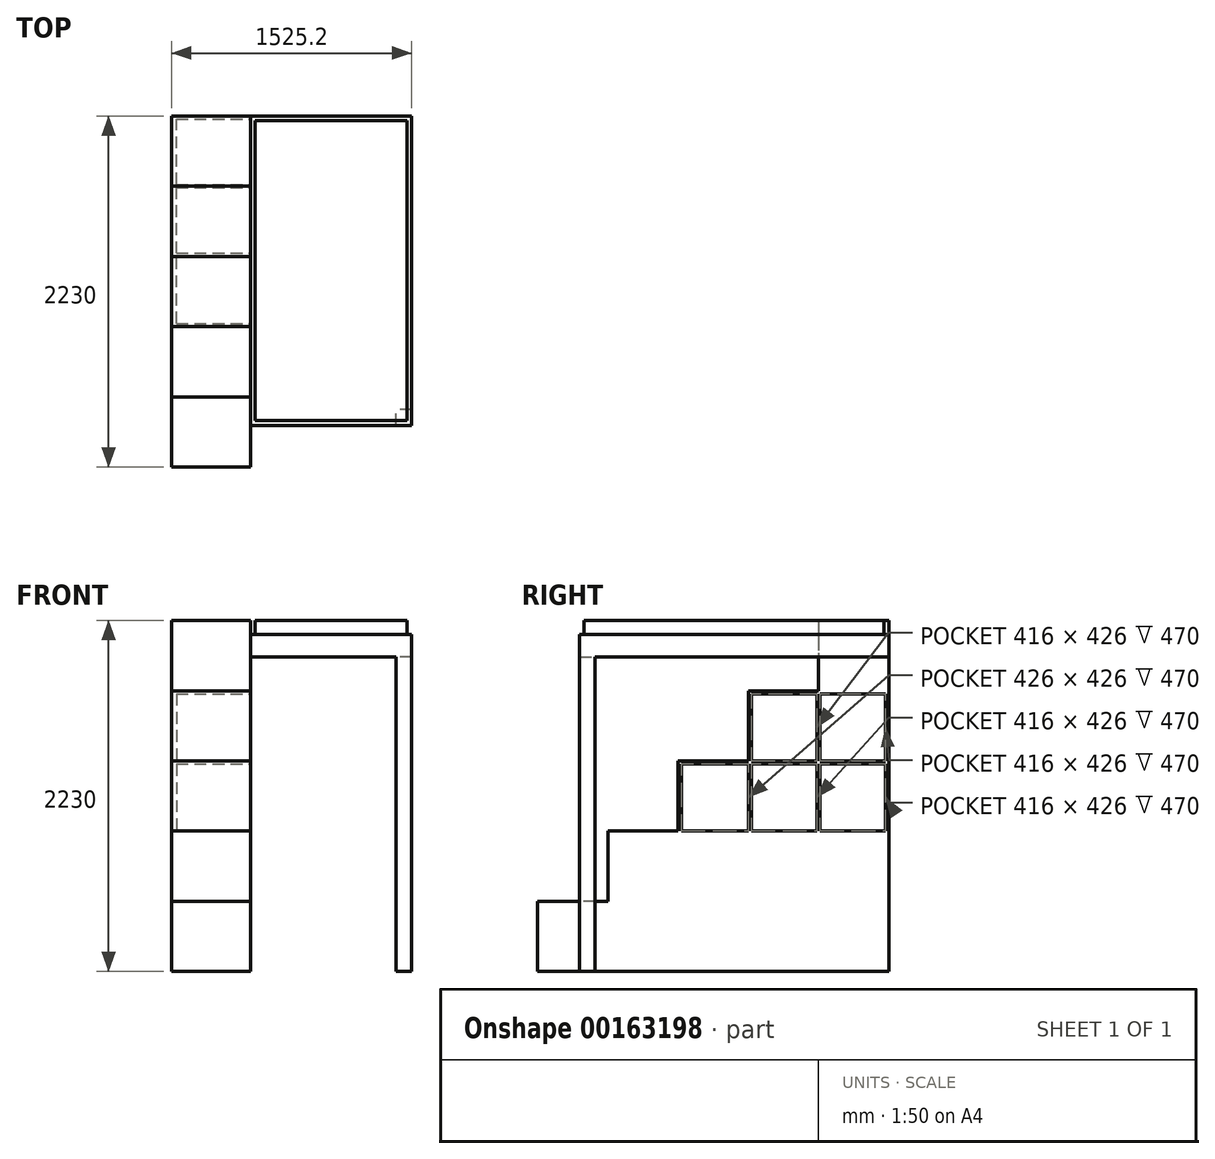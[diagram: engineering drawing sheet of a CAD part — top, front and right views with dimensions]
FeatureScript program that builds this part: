
annotation { "Feature Type Name" : "Feature", "Feature Type Description" : "" }
export const myFeature = defineFeature(function(context is Context, id is Id, definition is map)
    precondition{}
    {
        {
            var Q0;
            Q0=qCreatedBy(makeId("Top.planeOp"),FACE);
            var sketch = newSketch(context, id + "F0", { "sketchPlane" : qUnion([Q0])});
            skLineSegment(sketch, "E0.bottom", {"start": v(-482.6, 952.5) * mm, "end": v(482.6, 952.5) * mm});
            skLineSegment(sketch, "E0.top", {"start": v(-482.6, -952.5) * mm, "end": v(482.6, -952.5) * mm});
            skLineSegment(sketch, "E0.left", {"start": v(-482.6, 952.5) * mm, "end": v(-482.6, -952.5) * mm});
            skLineSegment(sketch, "E0.right", {"start": v(482.6, 952.5) * mm, "end": v(482.6, -952.5) * mm});
            skPoint(sketch, "E0.middle", {"position": v(0, 0) * mm});
            skSolve(sketch);
        }
        {
            var Q0;
            Q0 = qSketchRegion(id + "F0", true);
            extrude(context, id + "F1", {"entities" : qUnion([Q0]), "endBound" : BoundingType.SYMMETRIC, "depth" : 200 * mm});
        }
        {
            var Q0;
            Q0=makeQuery(id+"F1.opExtrude","CAP_FACE",FACE,{"disambiguationData":[OSD([sQuery(id+"F0.wireOp",EDGE,"E0.bottom"),sQuery(id+"F0.wireOp",EDGE,"E0.top"),sQuery(id+"F0.wireOp",EDGE,"E0.left"),sQuery(id+"F0.wireOp",EDGE,"E0.right")])],"isStart":true});
            var sketch = newSketch(context, id + "F2", { "sketchPlane" : qUnion([Q0])});
            skLineSegment(sketch, "E1.0.0", {"start": v(-482.6, -952.5) * mm, "end": v(482.6, -952.5) * mm});
            skLineSegment(sketch, "E1.0.1", {"start": v(482.6, -952.5) * mm, "end": v(482.6, 952.5) * mm});
            skLineSegment(sketch, "E1.0.2", {"start": v(482.6, 952.5) * mm, "end": v(-482.6, 952.5) * mm});
            skLineSegment(sketch, "E1.0.3", {"start": v(-482.6, 952.5) * mm, "end": v(-482.6, -952.5) * mm});
            skLineSegment(sketch, "E2.0", {"start": v(-512.6, -982.5) * mm, "end": v(512.6, -982.5) * mm});
            skLineSegment(sketch, "E2.1", {"start": v(-512.6, 982.5) * mm, "end": v(-512.6, -982.5) * mm});
            skLineSegment(sketch, "E2.2", {"start": v(512.6, 982.5) * mm, "end": v(-512.6, 982.5) * mm});
            skLineSegment(sketch, "E2.3", {"start": v(512.6, -982.5) * mm, "end": v(512.6, 982.5) * mm});
            skSolve(sketch);
        }
        {
            var Q0;
            Q0 = qSketchRegion(id + "F2", true);
            extrude(context, id + "F3", {"entities" : qUnion([Q0]), "oppositeDirection" : true, "depth" : 110 * mm});
        }
        {
            var Q0;
            Q0=makeQuery(id+"F3.opExtrude","CAP_FACE",FACE,{"disambiguationData":[OSD([sQuery(id+"F2.wireOp",EDGE,"E1.0.0"),sQuery(id+"F2.wireOp",EDGE,"E1.0.1"),sQuery(id+"F2.wireOp",EDGE,"E1.0.2"),sQuery(id+"F2.wireOp",EDGE,"E1.0.3"),sQuery(id+"F2.wireOp",EDGE,"E2.0"),sQuery(id+"F2.wireOp",EDGE,"E2.1"),sQuery(id+"F2.wireOp",EDGE,"E2.2"),sQuery(id+"F2.wireOp",EDGE,"E2.3")])],"isStart":true});
            var sketch = newSketch(context, id + "F4", { "sketchPlane" : qUnion([Q0])});
            skLineSegment(sketch, "E3.0", {"start": v(-512.6, 982.5) * mm, "end": v(-512.6, -982.5) * mm});
            skLineSegment(sketch, "E4.0", {"start": v(512.6, 982.5) * mm, "end": v(-512.6, 982.5) * mm});
            skLineSegment(sketch, "E5.0", {"start": v(512.6, -982.5) * mm, "end": v(512.6, 982.5) * mm});
            skLineSegment(sketch, "E6.0", {"start": v(-512.6, -982.5) * mm, "end": v(512.6, -982.5) * mm});
            skSolve(sketch);
        }
        {
            var Q0;
            Q0 = qSketchRegion(id + "F4", true);
            extrude(context, id + "F5", {"entities" : qUnion([Q0]), "operationType" : NewBodyOperationType.ADD, "depth" : 30 * mm});
        }
        {
            var Q0;
            Q0=makeQuery(id+"F5.boolean.opBoolean","MERGE",FACE,{"derivedFrom":[makeQuery(id+"F3.opExtrude","SWEPT_FACE",FACE,{"disambiguationData":[OSD([sQuery(id+"F2.wireOp",EDGE,"E2.1")])]}),makeQuery(id+"F5.opExtrude","SWEPT_FACE",FACE,{"disambiguationData":[OSD([sQuery(id+"F4.wireOp",EDGE,"E3.0")])]})]});
            var sketch = newSketch(context, id + "F6", { "sketchPlane" : qUnion([Q0])});
            skLineSegment(sketch, "E7", {"start": v(-982.5, 100) * mm, "end": v(-982.5, -2130) * mm});
            skLineSegment(sketch, "E8", {"start": v(-982.5, 100) * mm, "end": v(-536.5, 100) * mm});
            skLineSegment(sketch, "E9", {"start": v(-536.5, 100) * mm, "end": v(-536.5, -346) * mm});
            skLineSegment(sketch, "E10", {"start": v(-536.5, -346) * mm, "end": v(-90.5, -346) * mm});
            skLineSegment(sketch, "E11", {"start": v(-90.5, -346) * mm, "end": v(-90.5, -792) * mm});
            skLineSegment(sketch, "E12", {"start": v(-90.5, -792) * mm, "end": v(355.5, -792) * mm});
            skLineSegment(sketch, "E13", {"start": v(355.5, -792) * mm, "end": v(355.5, -1238) * mm});
            skLineSegment(sketch, "E14", {"start": v(355.5, -1238) * mm, "end": v(801.5, -1238) * mm});
            skLineSegment(sketch, "E15", {"start": v(801.5, -1238) * mm, "end": v(801.5, -1684) * mm});
            skLineSegment(sketch, "E16", {"start": v(801.5, -1684) * mm, "end": v(1247.5, -1684) * mm});
            skLineSegment(sketch, "E17", {"start": v(1247.5, -1684) * mm, "end": v(1247.5, -2130) * mm});
            skLineSegment(sketch, "E18", {"start": v(-982.5, -2130) * mm, "end": v(1247.5, -2130) * mm});
            skSolve(sketch);
        }
        {
            var Q0;
            Q0 = qSketchRegion(id + "F6", true);
            extrude(context, id + "F7", {"entities" : qUnion([Q0]), "operationType" : NewBodyOperationType.ADD, "depth" : 500 * mm});
        }
        {
            var Q0;
            Q0=makeQuery(id+"F5.opExtrude","CAP_FACE",FACE,{"disambiguationData":[OSD([sQuery(id+"F4.wireOp",EDGE,"E3.0"),sQuery(id+"F4.wireOp",EDGE,"E4.0"),sQuery(id+"F4.wireOp",EDGE,"E5.0"),sQuery(id+"F4.wireOp",EDGE,"E6.0")])],"isStart":false});
            var sketch = newSketch(context, id + "F8", { "sketchPlane" : qUnion([Q0])});
            skLineSegment(sketch, "E19.bottom", {"start": v(512.6, 982.5) * mm, "end": v(412.6, 982.5) * mm});
            skLineSegment(sketch, "E19.top", {"start": v(512.6, 882.5) * mm, "end": v(412.6, 882.5) * mm});
            skLineSegment(sketch, "E19.left", {"start": v(512.6, 982.5) * mm, "end": v(512.6, 882.5) * mm});
            skLineSegment(sketch, "E19.right", {"start": v(412.6, 982.5) * mm, "end": v(412.6, 882.5) * mm});
            skSolve(sketch);
        }
        {
            var Q0;
            Q0 = qSketchRegion(id + "F8", true);
            var Q1;
            Q1=makeQuery(id+"F7.opExtrude","SWEPT_FACE",FACE,{"disambiguationData":[OSD([sQuery(id+"F6.wireOp",EDGE,"E18")])]});
            extrude(context, id + "F9", {"entities" : qUnion([Q0]), "operationType" : NewBodyOperationType.ADD, "endBound" : BoundingType.UP_TO_SURFACE, "endBoundEntityFace" : qUnion([Q1]), "depth" : 25 * mm});
        }
        {
            var Q0;
            {var subQ0=sQuery(id+"F6.wireOp",EDGE,"E12");var subQ1=sQuery(id+"F6.wireOp",EDGE,"E11");var subQ2=sQuery(id+"F6.wireOp",EDGE,"E10");var subQ4=sQuery(id+"F6.wireOp",EDGE,"E7");var subQ6=sQuery(id+"F6.wireOp",EDGE,"E9");var subQ7=sQuery(id+"F6.wireOp",EDGE,"E16");var subQ8=sQuery(id+"F6.wireOp",EDGE,"E13");var subQ9=sQuery(id+"F6.wireOp",EDGE,"E14");var subQ10=sQuery(id+"F6.wireOp",EDGE,"E15");var subQ11=sQuery(id+"F6.wireOp",EDGE,"E17");var subQ12=sQuery(id+"F6.wireOp",EDGE,"E18");Q0=makeQuery(id+"F7.boolean.opBoolean","SPLIT",FACE,{"disambiguationData":[TD([makeQuery(id+"F7.opExtrude","SWEPT_FACE",FACE,{"disambiguationData":[OSD([subQ2])]})])],"derivedFrom":makeQuery(id+"F7.opExtrude","CAP_FACE",FACE,{"disambiguationData":[OSD([subQ4,sQuery(id+"F6.wireOp",EDGE,"E8"),subQ6,subQ2,subQ1,subQ0,subQ8,subQ9,subQ10,subQ7,subQ11,subQ12])],"isStart":true})});}
            var sketch = newSketch(context, id + "F10", { "sketchPlane" : qUnion([Q0])});
            skLineSegment(sketch, "E20.bottom", {"start": v(110.5, -366) * mm, "end": v(526.5, -366) * mm});
            skLineSegment(sketch, "E20.top", {"start": v(110.5, -792) * mm, "end": v(526.5, -792) * mm});
            skLineSegment(sketch, "E20.left", {"start": v(110.5, -366) * mm, "end": v(110.5, -792) * mm});
            skLineSegment(sketch, "E20.right", {"start": v(526.5, -366) * mm, "end": v(526.5, -792) * mm});
            skLineSegment(sketch, "E21.bottom", {"start": v(-335.5, -812) * mm, "end": v(90.5, -812) * mm});
            skLineSegment(sketch, "E21.top", {"start": v(-335.5, -1238) * mm, "end": v(90.5, -1238) * mm});
            skLineSegment(sketch, "E21.left", {"start": v(-335.5, -812) * mm, "end": v(-335.5, -1238) * mm});
            skLineSegment(sketch, "E21.right", {"start": v(90.5, -812) * mm, "end": v(90.5, -1238) * mm});
            skLineSegment(sketch, "E22.bottom", {"start": v(110.5, -812) * mm, "end": v(526.5, -812) * mm});
            skLineSegment(sketch, "E22.top", {"start": v(110.5, -1238) * mm, "end": v(526.5, -1238) * mm});
            skLineSegment(sketch, "E22.left", {"start": v(110.5, -812) * mm, "end": v(110.5, -1238) * mm});
            skLineSegment(sketch, "E22.right", {"start": v(526.5, -812) * mm, "end": v(526.5, -1238) * mm});
            skLineSegment(sketch, "E23.bottom", {"start": v(90.5, -792) * mm, "end": v(110.5, -792) * mm, "construction": true});
            skLineSegment(sketch, "E23.top", {"start": v(90.5, -812) * mm, "end": v(110.5, -812) * mm, "construction": true});
            skLineSegment(sketch, "E23.left", {"start": v(90.5, -792) * mm, "end": v(90.5, -812) * mm, "construction": true});
            skLineSegment(sketch, "E23.right", {"start": v(110.5, -792) * mm, "end": v(110.5, -812) * mm, "construction": true});
            skLineSegment(sketch, "E24.bottom", {"start": v(-335.5, -812) * mm, "end": v(-355.5, -812) * mm, "construction": true});
            skLineSegment(sketch, "E24.top", {"start": v(-335.5, -792) * mm, "end": v(-355.5, -792) * mm, "construction": true});
            skLineSegment(sketch, "E24.left", {"start": v(-335.5, -812) * mm, "end": v(-335.5, -792) * mm, "construction": true});
            skLineSegment(sketch, "E24.right", {"start": v(-355.5, -812) * mm, "end": v(-355.5, -792) * mm, "construction": true});
            skLineSegment(sketch, "E25.bottom", {"start": v(90.5, -346) * mm, "end": v(110.5, -346) * mm, "construction": true});
            skLineSegment(sketch, "E25.top", {"start": v(90.5, -366) * mm, "end": v(110.5, -366) * mm, "construction": true});
            skLineSegment(sketch, "E25.left", {"start": v(90.5, -346) * mm, "end": v(90.5, -366) * mm, "construction": true});
            skLineSegment(sketch, "E25.right", {"start": v(110.5, -346) * mm, "end": v(110.5, -366) * mm, "construction": true});
            skLineSegment(sketch, "E26.bottom", {"start": v(546.5, -366) * mm, "end": v(962.5, -366) * mm});
            skLineSegment(sketch, "E26.top", {"start": v(546.5, -792) * mm, "end": v(962.5, -792) * mm});
            skLineSegment(sketch, "E26.left", {"start": v(546.5, -366) * mm, "end": v(546.5, -792) * mm});
            skLineSegment(sketch, "E26.right", {"start": v(962.5, -366) * mm, "end": v(962.5, -792) * mm});
            skLineSegment(sketch, "E27.bottom", {"start": v(546.5, -812) * mm, "end": v(962.5, -812) * mm});
            skLineSegment(sketch, "E27.top", {"start": v(546.5, -1238) * mm, "end": v(962.5, -1238) * mm});
            skLineSegment(sketch, "E27.left", {"start": v(546.5, -812) * mm, "end": v(546.5, -1238) * mm});
            skLineSegment(sketch, "E27.right", {"start": v(962.5, -812) * mm, "end": v(962.5, -1238) * mm});
            skLineSegment(sketch, "E28", {"start": v(526.5, -366) * mm, "end": v(546.5, -366) * mm, "construction": true});
            skLineSegment(sketch, "E29", {"start": v(962.5, -366) * mm, "end": v(982.5, -366) * mm, "construction": true});
            skSolve(sketch);
        }
        {
            var Q0;
            Q0 = qSketchRegion(id + "F10", true);
            extrude(context, id + "F11", {"entities" : qUnion([Q0]), "operationType" : NewBodyOperationType.REMOVE, "oppositeDirection" : true, "depth" : 470 * mm});
        }
    });
